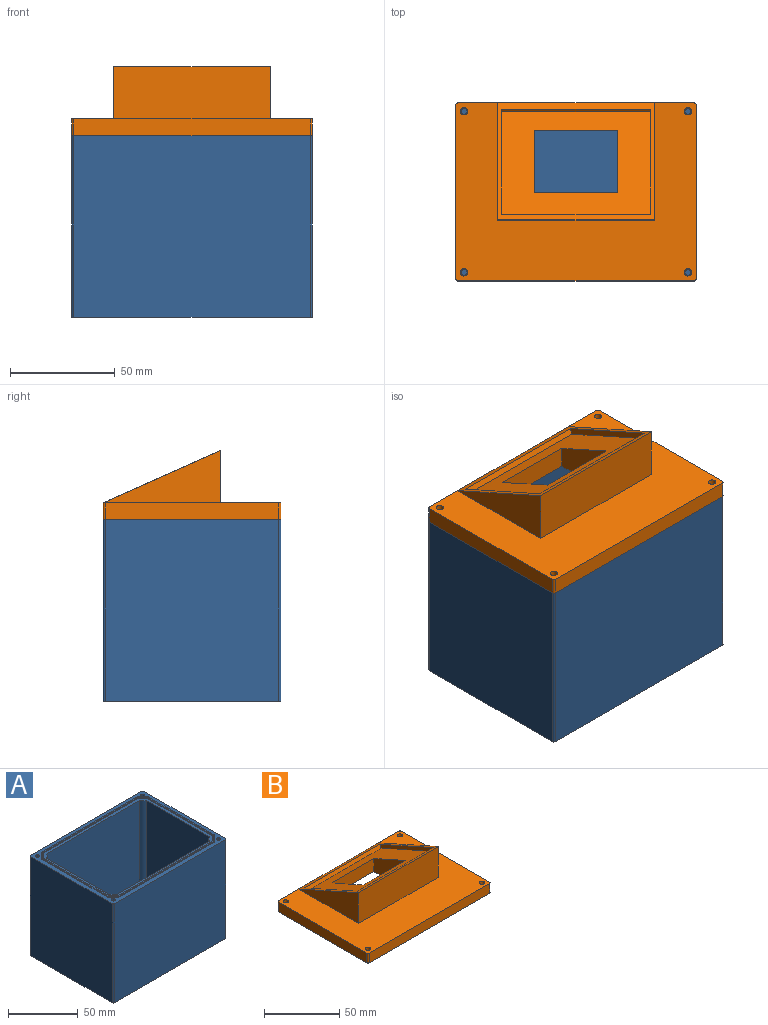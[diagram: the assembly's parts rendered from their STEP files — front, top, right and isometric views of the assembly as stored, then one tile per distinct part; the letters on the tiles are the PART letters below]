
ASSEMBLY  parts=2 mates=1
PART A: 77 faces, bbox 115x85x87.8 mm
  f0: cylinder r=1.5mm len=1.42mm, axis (0,0,1), area 1.5mm2, adj f11,f12,f38,f42
  f1: cylinder r=1.5mm len=1.42mm, axis (0,0,1), area 1.5mm2, adj f2,f12,f38,f42
  f2: plane 65.77x0.8mm, normal (1,0,0), area 52.6mm2, adj f1,f3,f12,f42
  f3: cylinder r=1.5mm len=1.42mm, axis (0,0,1), area 1.5mm2, adj f2,f12,f39,f42
  f4: cylinder r=1.5mm len=1.41mm, axis (0,0,1), area 1.5mm2, adj f5,f12,f39,f42
  f5: plane 95.79x0.8mm, normal (0,1,0), area 76.6mm2, adj f4,f6,f12,f42
  f6: cylinder r=1.5mm len=1.41mm, axis (0,0,1), area 1.5mm2, adj f5,f12,f40,f42
  f7: cylinder r=1.5mm len=1.42mm, axis (0,0,1), area 1.5mm2, adj f8,f12,f40,f42
  f8: plane 65.77x0.8mm, normal (-1,0,0), area 52.6mm2, adj f7,f9,f12,f42
  f9: cylinder r=1.5mm len=1.42mm, axis (0,0,1), area 1.5mm2, adj f8,f12,f41,f42
  f10: cylinder r=1.5mm len=1.42mm, axis (0,0,1), area 1.5mm2, adj f11,f12,f41,f42
  f11: plane 95.77x0.8mm, normal (0,-1,0), area 76.6mm2, adj f0,f10,f12,f42
  f12: plane 106.06x76.03mm, normal (0,0,1), area 808.2mm2, adj f0,f1,f2,f3,f4,f5,f6,f7
  f13: cylinder r=1.45mm len=9mm, axis (0,0,-1), area 82mm2, adj f20,f29
  f14: cylinder r=1.45mm len=9mm, axis (0,0,-1), area 82mm2, adj f18,f28
  f15: cylinder r=1.45mm len=9mm, axis (0,0,-1), area 82mm2, adj f24,f27
  f16: cylinder r=1.45mm len=9mm, axis (0,0,-1), area 82mm2, adj f22,f26
  f17: plane 101.4x71.4mm, normal (0,0,1), area 7006.1mm2, adj f19,f21,f23,f25,f30,f31,f32,f33
  f18: plane 8x8mm, normal (0,0,1), area 43.7mm2, adj f14,f19
  f19: cylinder r=4mm len=11mm, axis (0,0,-1), area 276.5mm2, adj f17,f18
  f20: plane 8x8mm, normal (0,0,1), area 43.7mm2, adj f13,f21
  f21: cylinder r=4mm len=11mm, axis (0,0,-1), area 276.5mm2, adj f17,f20
  f22: plane 8x8mm, normal (0,0,1), area 43.7mm2, adj f16,f23
  f23: cylinder r=4mm len=11mm, axis (0,0,-1), area 276.5mm2, adj f17,f22
  f24: plane 8x8mm, normal (0,0,1), area 43.7mm2, adj f15,f25
  f25: cylinder r=4mm len=11mm, axis (0,0,-1), area 276.5mm2, adj f17,f24
  f26: plane 2.9x2.9mm, normal (0,0,1), area 6.6mm2, adj f16
  f27: plane 2.9x2.9mm, normal (0,0,1), area 6.6mm2, adj f15
  f28: plane 2.9x2.9mm, normal (0,0,1), area 6.6mm2, adj f14
  f29: plane 2.9x2.9mm, normal (0,0,1), area 6.6mm2, adj f13
  f30: plane 85x64.17mm, normal (-1,0,0), area 5454.3mm2, adj f12,f17,f31,f37
  f31: cylinder r=7mm len=85mm, axis (0,0,-1), area 444.9mm2, adj f12,f17,f30,f32
  f32: plane 94.17x85mm, normal (0,1,0), area 8004.3mm2, adj f12,f17,f31,f33
  f33: cylinder r=7mm len=85mm, axis (0,0,-1), area 444.9mm2, adj f12,f17,f32,f34
  f34: plane 85x64.17mm, normal (1,0,0), area 5454.3mm2, adj f12,f17,f33,f35
  f35: cylinder r=7mm len=85mm, axis (0,0,-1), area 444.9mm2, adj f12,f17,f34,f36
  f36: plane 94.17x85mm, normal (0,-1,0), area 8004.3mm2, adj f12,f17,f35,f37
  f37: cylinder r=7mm len=85mm, axis (0,0,-1), area 444.9mm2, adj f12,f17,f30,f36
  f38: cylinder r=4.45mm len=2.72mm, axis (0,0,1), area 3.2mm2, adj f0,f1,f12,f42
  f39: cylinder r=4.45mm len=2.72mm, axis (0,0,1), area 3.2mm2, adj f3,f4,f12,f42
  f40: cylinder r=4.45mm len=2.72mm, axis (0,0,1), area 3.2mm2, adj f6,f7,f12,f42
  f41: cylinder r=4.45mm len=2.72mm, axis (0,0,1), area 3.2mm2, adj f9,f10,f12,f42
  f42: plane 108.06x78.03mm, normal (0,0,1), area 356.9mm2, adj f0,f1,f2,f3,f4,f5,f6,f7
  f43: plane 115x85mm, normal (0,0,-1), area 9774.1mm2, adj f48,f49,f50,f51,f52,f53,f54,f55
  f44: plane 2.9x2.9mm, normal (0,0,1), area 6.6mm2, adj f56
  f45: plane 2.9x2.9mm, normal (0,0,1), area 6.6mm2, adj f57
  f46: plane 2.9x2.9mm, normal (0,0,1), area 6.6mm2, adj f58
  f47: plane 2.9x2.9mm, normal (0,0,1), area 6.6mm2, adj f59
  f48: cylinder r=1mm len=87mm, axis (0,0,-1), area 136.7mm2, adj f43,f49,f55,f60
  f49: plane 87x83mm, normal (1,0,0), area 7221mm2, adj f43,f48,f50,f60
  f50: cylinder r=1mm len=87mm, axis (0,0,-1), area 136.7mm2, adj f43,f49,f51,f60
  f51: plane 113x87mm, normal (0,-1,0), area 9831mm2, adj f43,f50,f52,f60
  f52: cylinder r=1mm len=87mm, axis (0,0,-1), area 136.7mm2, adj f43,f51,f53,f60
  f53: plane 87x83mm, normal (-1,0,0), area 7221mm2, adj f43,f52,f54,f60
  f54: cylinder r=1mm len=87mm, axis (0,0,-1), area 136.7mm2, adj f43,f53,f55,f60
  f55: plane 113x87mm, normal (0,1,0), area 9831mm2, adj f43,f48,f54,f60
  f56: cylinder r=1.45mm len=25mm, axis (0,0,1), area 227.8mm2, adj f44,f60
  f57: cylinder r=1.45mm len=25mm, axis (0,0,1), area 227.8mm2, adj f45,f60
  f58: cylinder r=1.45mm len=25mm, axis (0,0,1), area 227.8mm2, adj f46,f60
  f59: cylinder r=1.45mm len=25mm, axis (0,0,1), area 227.8mm2, adj f47,f60
  f60: plane 115x85mm, normal (0,0,1), area 1375.4mm2, adj f48,f49,f50,f51,f52,f53,f54,f55
  f61: plane 65.77x0.8mm, normal (1,0,0), area 52.6mm2, adj f42,f60,f62,f76
  f62: cylinder r=2.5mm len=2.36mm, axis (0,0,1), area 2.5mm2, adj f42,f60,f61,f63
  f63: cylinder r=3.45mm len=2.11mm, axis (0,0,1), area 2.5mm2, adj f42,f60,f62,f64
  f64: cylinder r=2.5mm len=2.36mm, axis (0,0,1), area 2.5mm2, adj f42,f60,f63,f65
  f65: plane 95.77x0.8mm, normal (0,1,0), area 76.6mm2, adj f42,f60,f64,f66
  f66: cylinder r=2.5mm len=2.36mm, axis (0,0,1), area 2.5mm2, adj f42,f60,f65,f67
  f67: cylinder r=3.45mm len=2.11mm, axis (0,0,1), area 2.5mm2, adj f42,f60,f66,f68
  f68: cylinder r=2.5mm len=2.36mm, axis (0,0,1), area 2.5mm2, adj f42,f60,f67,f69
  f69: plane 65.77x0.8mm, normal (-1,0,0), area 52.6mm2, adj f42,f60,f68,f70
  f70: cylinder r=2.5mm len=2.36mm, axis (0,0,1), area 2.5mm2, adj f42,f60,f69,f71
  f71: cylinder r=3.45mm len=2.11mm, axis (0,0,1), area 2.5mm2, adj f42,f60,f70,f72
  f72: cylinder r=2.5mm len=2.35mm, axis (0,0,1), area 2.5mm2, adj f42,f60,f71,f73
  f73: plane 95.79x0.8mm, normal (0,-1,0), area 76.6mm2, adj f42,f60,f72,f74
  f74: cylinder r=2.5mm len=2.35mm, axis (0,0,1), area 2.5mm2, adj f42,f60,f73,f75
  f75: cylinder r=3.45mm len=2.11mm, axis (0,0,1), area 2.5mm2, adj f42,f60,f74,f76
  f76: cylinder r=2.5mm len=2.36mm, axis (0,0,1), area 2.5mm2, adj f42,f60,f61,f75
PART B: 61 faces, bbox 115x85x33 mm
  f0: plane 115x85mm, normal (0,0,-1), area 1177mm2, adj f1,f4,f5,f6,f7,f8,f9,f10
  f1: plane 113x8mm, normal (0,1,0), area 904mm2, adj f0,f3,f4,f14,f22
  f2: plane 105.19x75.19mm, normal (0,0,-1), area 6657.4mm2, adj f18,f19,f20,f21,f28,f29,f30,f31
  f3: plane 115x85mm, normal (0,0,1), area 5535.7mm2, adj f1,f4,f5,f6,f7,f8,f9,f10
  f4: cylinder r=1mm len=8mm, axis (0,0,-1), area 12.6mm2, adj f0,f1,f3,f5
  f5: plane 83x8mm, normal (-1,0,0), area 664mm2, adj f0,f3,f4,f6
  f6: cylinder r=1mm len=8mm, axis (0,0,-1), area 12.6mm2, adj f0,f3,f5,f7
  f7: plane 113x8mm, normal (0,-1,0), area 904mm2, adj f0,f3,f6,f8
  f8: cylinder r=1mm len=8mm, axis (0,0,-1), area 12.6mm2, adj f0,f3,f7,f9
  f9: plane 83x8mm, normal (1,0,0), area 664mm2, adj f0,f3,f8,f14
  f10: cylinder r=1.75mm len=8mm, axis (0,0,-1), area 88mm2, adj f0,f3
  f11: cylinder r=1.75mm len=8mm, axis (0,0,-1), area 88mm2, adj f0,f3
  f12: cylinder r=1.75mm len=8mm, axis (0,0,-1), area 88mm2, adj f0,f3
  f13: cylinder r=1.75mm len=8mm, axis (0,0,-1), area 88mm2, adj f0,f3
  f14: cylinder r=1mm len=8mm, axis (0,0,-1), area 12.6mm2, adj f0,f1,f3,f9
  f15: plane 56x25mm, normal (1,0,0), area 700mm2, adj f3,f17,f22
  f16: plane 56x25mm, normal (-1,0,0), area 700mm2, adj f3,f17,f22
  f17: plane 75x25mm, normal (0,-1,0), area 1875mm2, adj f3,f15,f16,f22
  f18: plane 40x23.91mm, normal (0,1,0), area 956.4mm2, adj f2,f19,f21,f27
  f19: plane 30x23.91mm, normal (1,0,0), area 516.4mm2, adj f2,f18,f20,f27
  f20: plane 40x10.52mm, normal (0,-1,0), area 420.7mm2, adj f2,f19,f21,f27
  f21: plane 30x23.91mm, normal (-1,0,0), area 516.4mm2, adj f2,f18,f20,f27
  f22: plane 75x56mm, normal (0,0.41,0.91), area 694.5mm2, adj f1,f15,f16,f17,f23,f24,f25,f26
  f23: plane 51.45x25.16mm, normal (1,0,0), area 165mm2, adj f22,f24,f26,f27
  f24: plane 71x2.74mm, normal (0,-0.91,0.41), area 213mm2, adj f22,f23,f25,f27
  f25: plane 51.45x25.16mm, normal (-1,0,0), area 165mm2, adj f22,f24,f26,f27
  f26: plane 71x2.74mm, normal (0,0.91,-0.41), area 213mm2, adj f22,f23,f25,f27
  f27: plane 71x50.22mm, normal (0,0.41,0.91), area 2590.9mm2, adj f18,f19,f20,f21,f23,f24,f25,f26
  f28: cylinder r=3mm len=2.62mm, axis (0,0,-1), area 4.8mm2, adj f2,f29,f59,f60
  f29: cylinder r=5.05mm len=1.97mm, axis (0,0,-1), area 4.2mm2, adj f2,f28,f30,f60
  f30: cylinder r=3mm len=2.79mm, axis (0,0,-1), area 5mm2, adj f2,f29,f31,f60
  f31: plane 92.81x1.5mm, normal (0,-1,0), area 139.2mm2, adj f2,f30,f32,f60
  f32: cylinder r=3mm len=2.62mm, axis (0,0,-1), area 4.8mm2, adj f2,f31,f33,f60
  f33: cylinder r=5mm len=1.92mm, axis (0,0,-1), area 4.1mm2, adj f2,f32,f34,f60
  f34: cylinder r=3mm len=2.62mm, axis (0,0,-1), area 4.8mm2, adj f2,f33,f35,f60
  f35: plane 62.98x1.5mm, normal (-1,0,0), area 94.5mm2, adj f2,f34,f36,f60
  f36: cylinder r=3mm len=2.62mm, axis (0,0,-1), area 4.8mm2, adj f2,f35,f37,f60
  f37: cylinder r=5.05mm len=1.97mm, axis (0,0,-1), area 4.2mm2, adj f2,f36,f38,f60
  f38: cylinder r=3mm len=2.62mm, axis (0,0,-1), area 4.8mm2, adj f2,f37,f39,f60
  f39: plane 92.92x1.5mm, normal (0,1,0), area 139.4mm2, adj f2,f38,f40,f60
  f40: cylinder r=3mm len=2.62mm, axis (0,0,-1), area 4.8mm2, adj f2,f39,f41,f60
  f41: cylinder r=5.05mm len=1.97mm, axis (0,0,-1), area 4.2mm2, adj f2,f40,f42,f60
  f42: cylinder r=3mm len=2.62mm, axis (0,0,-1), area 4.8mm2, adj f2,f41,f59,f60
  f43: cylinder r=3.05mm len=1.9mm, axis (0,0,-1), area 4.2mm2, adj f0,f44,f58,f60
  f44: cylinder r=3mm len=2.84mm, axis (0,0,-1), area 5.6mm2, adj f0,f43,f45,f60
  f45: plane 65.54x1.5mm, normal (-1,0,0), area 98.3mm2, adj f0,f44,f46,f60
  f46: cylinder r=3mm len=2.84mm, axis (0,0,-1), area 5.6mm2, adj f0,f45,f47,f60
  f47: cylinder r=3.05mm len=1.91mm, axis (0,0,-1), area 4.2mm2, adj f0,f46,f48,f60
  f48: cylinder r=3mm len=2.84mm, axis (0,0,-1), area 5.6mm2, adj f0,f47,f49,f60
  f49: plane 95.54x1.5mm, normal (0,-1,0), area 143.3mm2, adj f0,f48,f50,f60
  f50: cylinder r=3mm len=2.84mm, axis (0,0,-1), area 5.6mm2, adj f0,f49,f51,f60
  f51: cylinder r=3.05mm len=1.91mm, axis (0,0,-1), area 4.2mm2, adj f0,f50,f52,f60
  f52: cylinder r=3mm len=2.84mm, axis (0,0,-1), area 5.6mm2, adj f0,f51,f53,f60
  f53: plane 65.54x1.5mm, normal (1,0,0), area 98.3mm2, adj f0,f52,f54,f60
  f54: cylinder r=3mm len=2.84mm, axis (0,0,-1), area 5.6mm2, adj f0,f53,f55,f60
  f55: cylinder r=3.05mm len=1.9mm, axis (0,0,-1), area 4.2mm2, adj f0,f54,f56,f60
  f56: cylinder r=3mm len=2.83mm, axis (0,0,-1), area 5.6mm2, adj f0,f55,f57,f60
  f57: plane 95.58x1.5mm, normal (0,1,0), area 143.4mm2, adj f0,f56,f58,f60
  f58: cylinder r=3mm len=2.83mm, axis (0,0,-1), area 5.6mm2, adj f0,f43,f57,f60
  f59: plane 62.92x1.5mm, normal (1,0,0), area 94.4mm2, adj f2,f28,f42,f60
  f60: plane 109.13x79.06mm, normal (0,0,-1), area 701.4mm2, adj f28,f29,f30,f31,f32,f33,f34,f35
PLACE A t=(-52.6,-3.88,-6.19)mm
PLACE B t=(-55.1,-6.38,80.81)mm
MATE parallel B.f0 <-> A.f60  axis (0,0,-1) through (-50.67,38.62,80.81)mm
